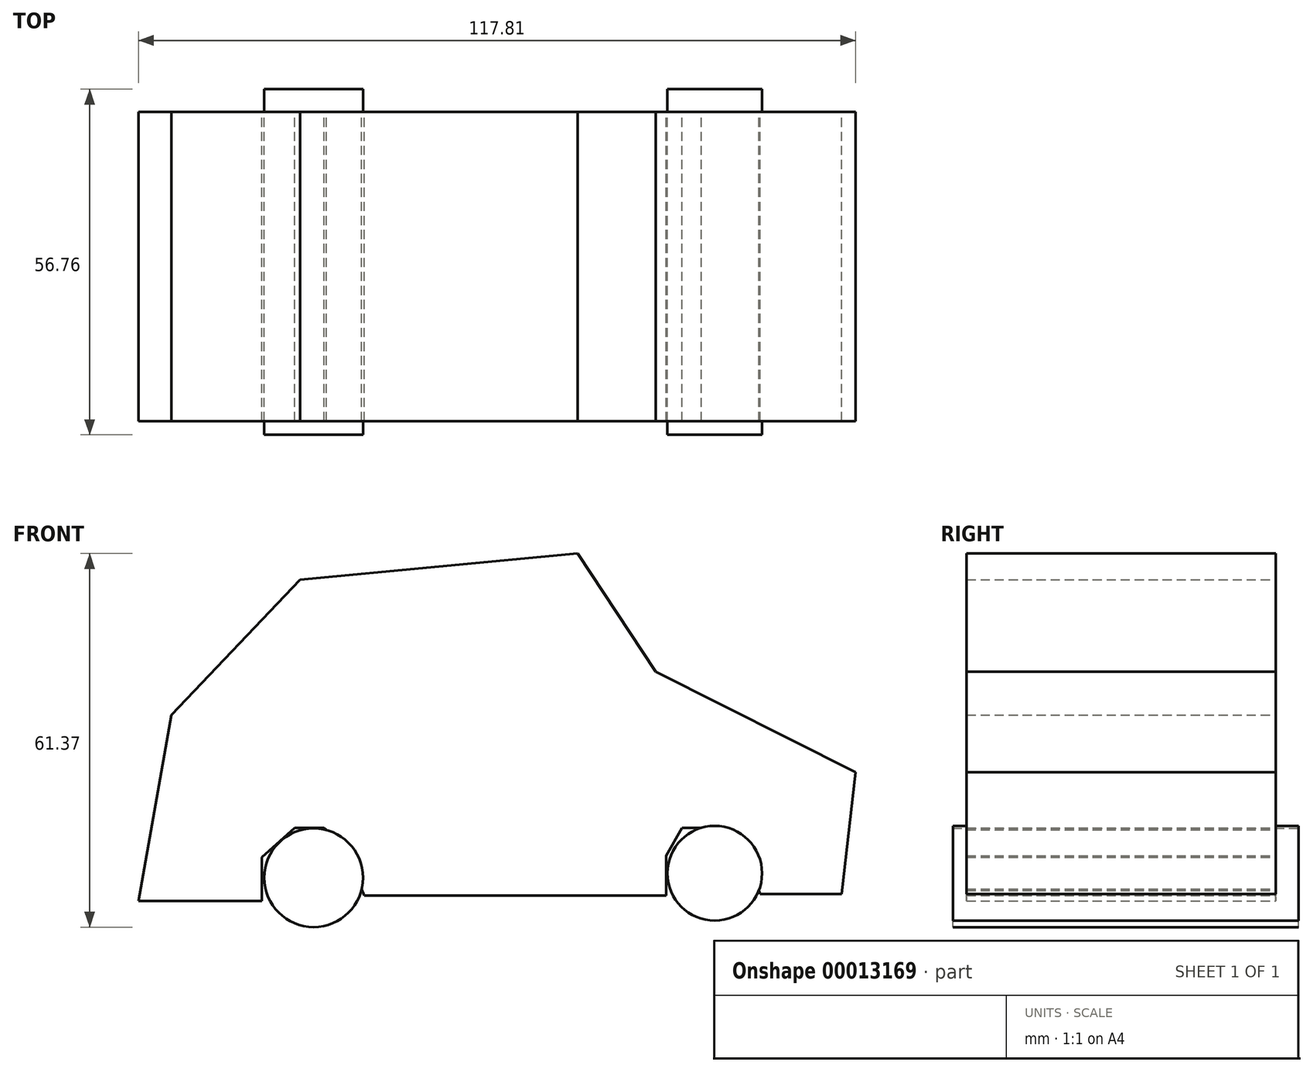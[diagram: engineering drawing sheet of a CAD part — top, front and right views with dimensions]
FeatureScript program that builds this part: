
annotation { "Feature Type Name" : "Feature", "Feature Type Description" : "" }
export const myFeature = defineFeature(function(context is Context, id is Id, definition is map)
    precondition{}
    {
        {
            var Q0;
            Q0=qCreatedBy(makeId("Front.planeOp"),FACE);
            var sketch = newSketch(context, id + "F0", { "sketchPlane" : qUnion([Q0])});
            skLineSegment(sketch, "E0", {"start": v(-58.7, -24.39) * mm, "end": v(-46.43, -24.39) * mm});
            skLineSegment(sketch, "E1", {"start": v(-46.43, -24.39) * mm, "end": v(-46.43, -17.26) * mm});
            skLineSegment(sketch, "E2", {"start": v(-46.43, -17.26) * mm, "end": v(-41.01, -12.4) * mm});
            skLineSegment(sketch, "E3", {"start": v(-41.01, -12.4) * mm, "end": v(-36.17, -12.4) * mm});
            skLineSegment(sketch, "E4", {"start": v(-36.17, -12.4) * mm, "end": v(-32.17, -16.4) * mm});
            skLineSegment(sketch, "E5", {"start": v(-32.17, -16.4) * mm, "end": v(-29.6, -23.53) * mm});
            skLineSegment(sketch, "E6", {"start": v(-29.6, -23.53) * mm, "end": v(20.03, -23.53) * mm});
            skLineSegment(sketch, "E7", {"start": v(20.03, -23.53) * mm, "end": v(20.03, -16.97) * mm});
            skLineSegment(sketch, "E8", {"start": v(20.03, -16.97) * mm, "end": v(22.6, -12.4) * mm});
            skLineSegment(sketch, "E9", {"start": v(22.6, -12.4) * mm, "end": v(28.3, -12.4) * mm});
            skLineSegment(sketch, "E10", {"start": v(28.3, -12.4) * mm, "end": v(33.15, -17.54) * mm});
            skLineSegment(sketch, "E11", {"start": v(33.15, -17.54) * mm, "end": v(35.43, -23.25) * mm});
            skLineSegment(sketch, "E12", {"start": v(35.43, -23.25) * mm, "end": v(48.84, -23.25) * mm});
            skLineSegment(sketch, "E13", {"start": v(48.84, -23.25) * mm, "end": v(51.12, -3.28) * mm});
            skLineSegment(sketch, "E14", {"start": v(51.12, -3.28) * mm, "end": v(18.32, 13.26) * mm});
            skLineSegment(sketch, "E15", {"start": v(18.32, 13.26) * mm, "end": v(5.48, 32.66) * mm});
            skLineSegment(sketch, "E16", {"start": v(5.48, 32.66) * mm, "end": v(-40.16, 28.38) * mm});
            skLineSegment(sketch, "E17", {"start": v(-40.16, 28.38) * mm, "end": v(-61.27, 6.13) * mm});
            skLineSegment(sketch, "E18", {"start": v(-61.27, 6.13) * mm, "end": v(-66.69, -24.39) * mm});
            skLineSegment(sketch, "E19", {"start": v(-66.69, -24.39) * mm, "end": v(-58.7, -24.39) * mm});
            skSolve(sketch);
        }
        {
            var Q0;
            Q0=makeQuery(id+"F0.imprint","IMPRINT",FACE,{"disambiguationData":[TD([[makeQuery(id+"F0.imprint","IMPRINT",EDGE,{"derivedFrom":sQuery(id+"F0.wireOp",EDGE,"E0")}),1.0]])]});
            extrude(context, id + "F1", {"entities" : qUnion([Q0]), "depth" : 25.4 * mm, "hasSecondDirection" : true, "secondDirectionOppositeDirection" : true, "secondDirectionDepth" : 25.4 * mm});
        }
        {
            var Q0;
            Q0=qCreatedBy(makeId("Front.planeOp"),FACE);
            var sketch = newSketch(context, id + "F2", { "sketchPlane" : qUnion([Q0])});
            skCircle(sketch, "E20", {"center": v(-37.9, -20.6) * mm, "radius": 8.1 * mm});
            skPoint(sketch, "E20.first.point", {"position": v(-45.3, -17.26) * mm});
            skPoint(sketch, "E20.second.point", {"position": v(-30.46, -23.82) * mm});
            skPoint(sketch, "E20.third.point", {"position": v(-43.58, -26.38) * mm});
            skCircle(sketch, "E21", {"center": v(27.98, -19.87) * mm, "radius": 7.78 * mm});
            skPoint(sketch, "E21.first.point", {"position": v(20.88, -16.69) * mm});
            skPoint(sketch, "E21.second.point", {"position": v(35.43, -22.1) * mm});
            skPoint(sketch, "E21.third.point", {"position": v(23.73, -26.38) * mm});
            skSolve(sketch);
        }
        {
            var Q0;
            Q0=makeQuery(id+"F2.imprint","IMPRINT",FACE,{"disambiguationData":[TD([[makeQuery(id+"F2.imprint","IMPRINT",EDGE,{"derivedFrom":sQuery(id+"F2.wireOp",EDGE,"E20")}),1.0]])]});
            var Q1;
            Q1=makeQuery(id+"F2.imprint","IMPRINT",FACE,{"disambiguationData":[TD([[makeQuery(id+"F2.imprint","IMPRINT",EDGE,{"derivedFrom":sQuery(id+"F2.wireOp",EDGE,"E21")}),1.0]])]});
            extrude(context, id + "F3", {"entities" : qUnion([Q0, Q1]), "operationType" : NewBodyOperationType.ADD, "depth" : 27.65 * mm, "hasSecondDirection" : true, "secondDirectionOppositeDirection" : true, "secondDirectionDepth" : 29.1 * mm});
        }
    });
